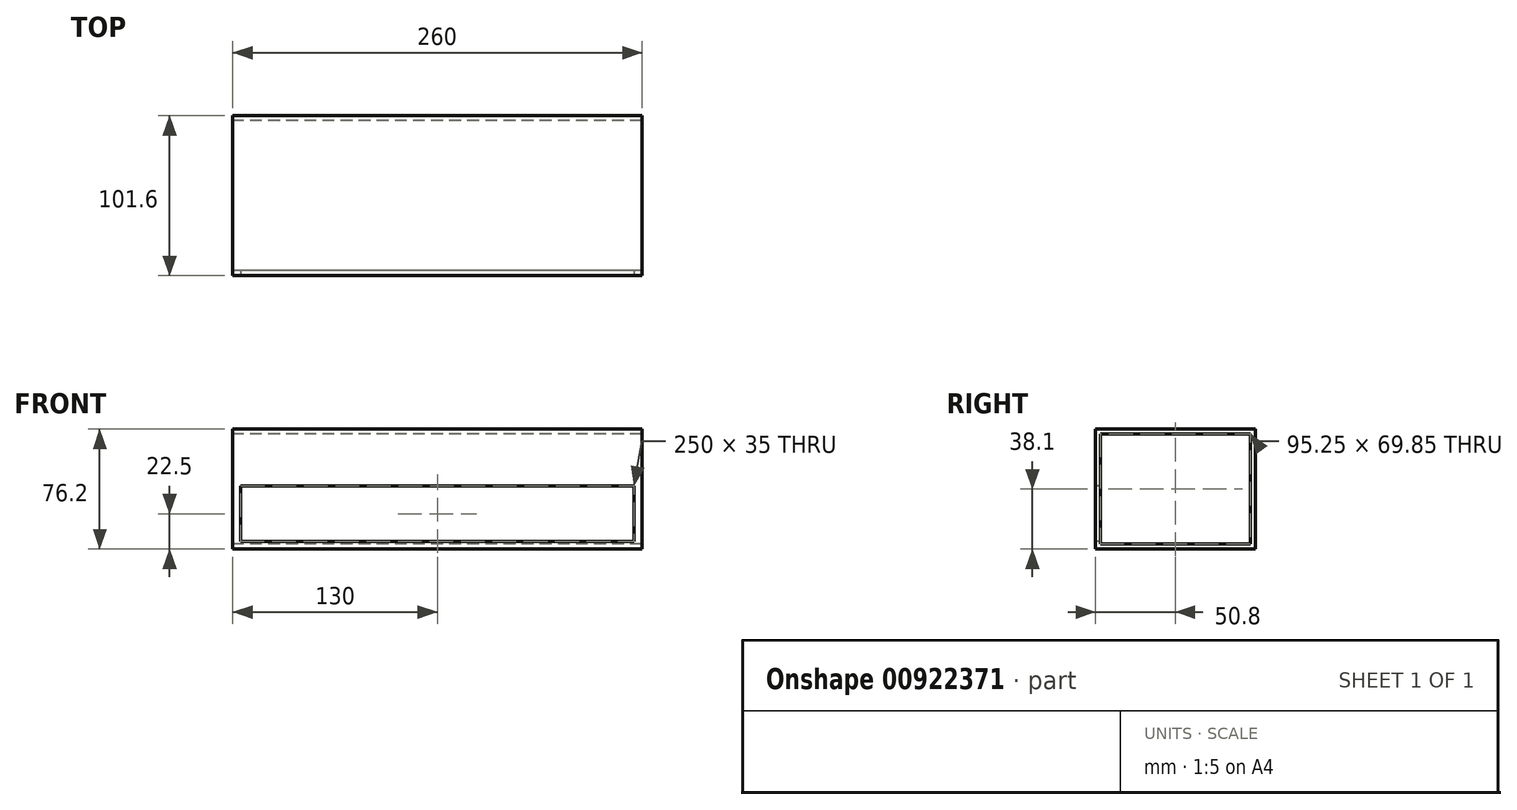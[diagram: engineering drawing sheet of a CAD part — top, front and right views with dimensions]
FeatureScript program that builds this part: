
annotation { "Feature Type Name" : "Feature", "Feature Type Description" : "" }
export const myFeature = defineFeature(function(context is Context, id is Id, definition is map)
    precondition{}
    {
        {
            var Q0;
            Q0=qCreatedBy(makeId("Right.planeOp"),FACE);
            var sketch = newSketch(context, id + "F0", { "sketchPlane" : qUnion([Q0])});
            skLineSegment(sketch, "E0.bottom", {"start": v(47.62, 34.93) * mm, "end": v(-47.63, 34.93) * mm});
            skLineSegment(sketch, "E0.top", {"start": v(47.63, -34.93) * mm, "end": v(-47.62, -34.93) * mm});
            skLineSegment(sketch, "E0.left", {"start": v(47.62, 34.92) * mm, "end": v(47.63, -34.93) * mm});
            skLineSegment(sketch, "E0.right", {"start": v(-47.63, 34.93) * mm, "end": v(-47.62, -34.93) * mm});
            skPoint(sketch, "E0.middle", {"position": v(0, 0) * mm});
            skLineSegment(sketch, "E1.bottom", {"start": v(50.8, 38.1) * mm, "end": v(-50.8, 38.1) * mm});
            skLineSegment(sketch, "E1.top", {"start": v(50.8, -38.1) * mm, "end": v(-50.8, -38.1) * mm});
            skLineSegment(sketch, "E1.left", {"start": v(50.8, 38.1) * mm, "end": v(50.8, -38.1) * mm});
            skLineSegment(sketch, "E1.right", {"start": v(-50.8, 38.1) * mm, "end": v(-50.8, -38.1) * mm});
            skSolve(sketch);
        }
        {
            var Q0;
            Q0 = qSketchRegion(id + "F0", true);
            extrude(context, id + "F1", {"entities" : qUnion([Q0]), "endBound" : BoundingType.SYMMETRIC, "depth" : 260 * mm, "offsetDistance" : 25 * mm, "hasSecondDirection" : true, "secondDirectionOppositeDirection" : true, "secondDirectionDepth" : 25 * mm});
        }
        {
            var Q0;
            Q0=makeQuery(id+"F1.opExtrude","SWEPT_FACE",FACE,{"disambiguationData":[OSD([sQuery(id+"F0.wireOp",EDGE,"E1.right")])]});
            var sketch = newSketch(context, id + "F2", { "sketchPlane" : qUnion([Q0])});
            skLineSegment(sketch, "E2.bottom", {"start": v(125, 1.9) * mm, "end": v(-125, 1.9) * mm});
            skLineSegment(sketch, "E2.top", {"start": v(125, -33.1) * mm, "end": v(-125, -33.1) * mm});
            skLineSegment(sketch, "E2.left", {"start": v(125, 1.9) * mm, "end": v(125, -33.1) * mm});
            skLineSegment(sketch, "E2.right", {"start": v(-125, 1.9) * mm, "end": v(-125, -33.1) * mm});
            skPoint(sketch, "E2.middle", {"position": v(0, -15.6) * mm});
            skSolve(sketch);
        }
        {
            var Q0;
            Q0 = qSketchRegion(id + "F2", true);
            extrude(context, id + "F3", {"entities" : qUnion([Q0]), "operationType" : NewBodyOperationType.REMOVE, "endBound" : BoundingType.UP_TO_NEXT, "oppositeDirection" : true, "depth" : 25 * mm, "offsetDistance" : 25 * mm});
        }
    });
